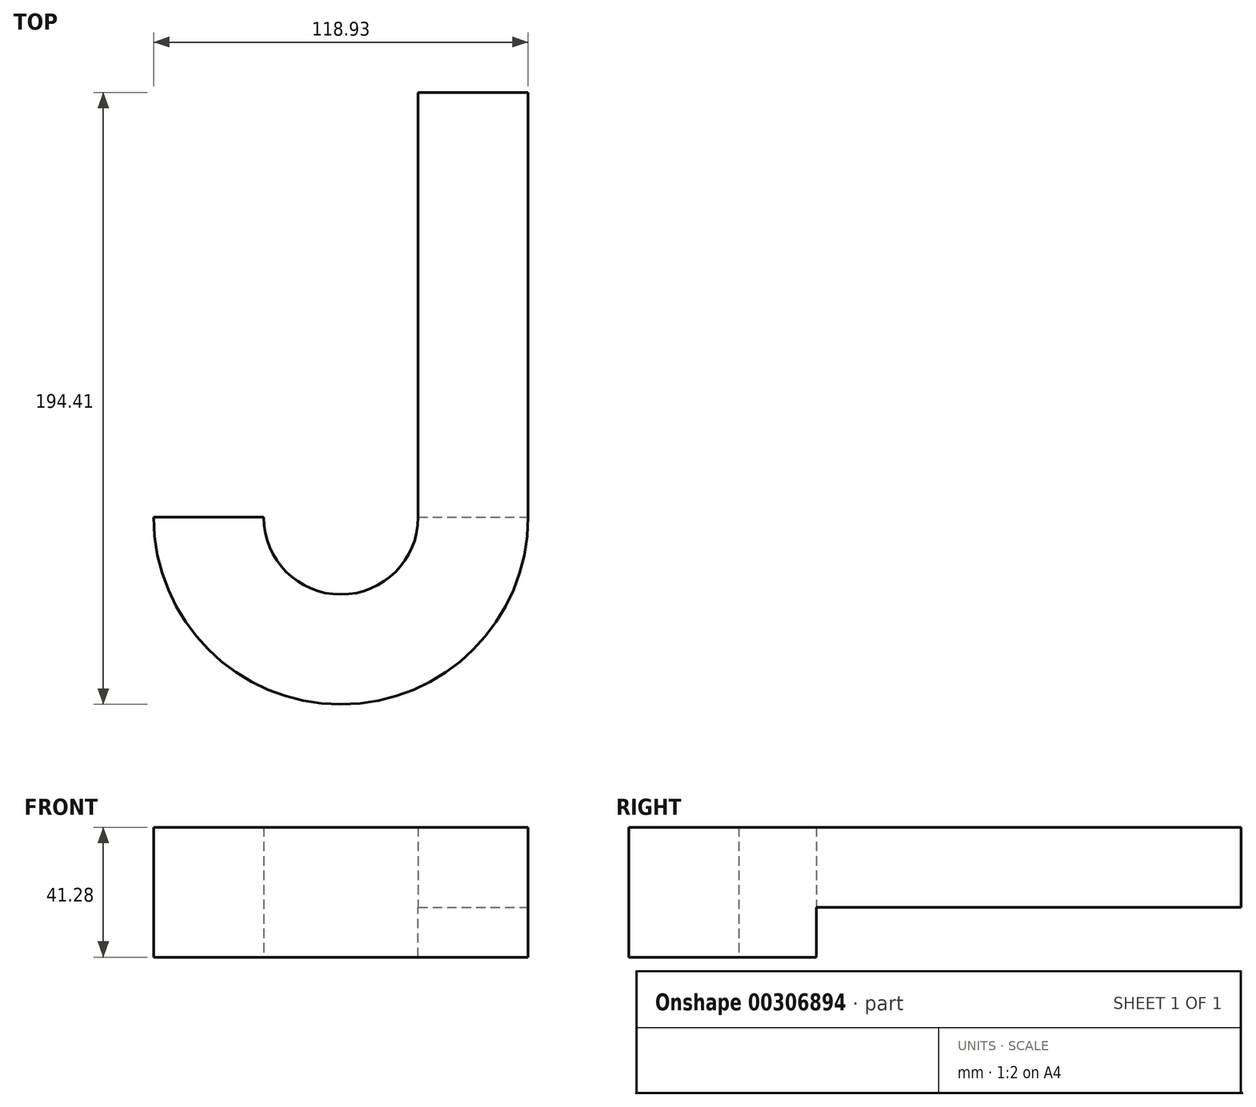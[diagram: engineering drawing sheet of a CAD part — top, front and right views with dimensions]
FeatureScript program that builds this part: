
annotation { "Feature Type Name" : "Feature", "Feature Type Description" : "" }
export const myFeature = defineFeature(function(context is Context, id is Id, definition is map)
    precondition{}
    {
        {
            var Q0;
            Q0=qCreatedBy(makeId("Top.planeOp"),FACE);
            var sketch = newSketch(context, id + "F0", { "sketchPlane" : qUnion([Q0])});
            skLineSegment(sketch, "E0.bottom", {"start": v(-17.46, 67.47) * mm, "end": v(17.46, 67.47) * mm});
            skLineSegment(sketch, "E0.top", {"start": v(-17.46, -67.47) * mm, "end": v(17.46, -67.47) * mm});
            skLineSegment(sketch, "E0.left", {"start": v(-17.46, 67.47) * mm, "end": v(-17.46, -67.47) * mm});
            skLineSegment(sketch, "E0.right", {"start": v(17.46, 67.47) * mm, "end": v(17.46, -67.47) * mm});
            skPoint(sketch, "E0.middle", {"position": v(0, 0) * mm});
            skArc(sketch, "E1", {"start": v(17.46, -67.47) * mm, "mid": v(-42, -126.94) * mm, "end": v(-101.47, -67.47) * mm});
            skArc(sketch, "E2.0", {"start": v(-17.46, -67.47) * mm, "mid": v(-42, -92.01) * mm, "end": v(-66.55, -67.47) * mm});
            skLineSegment(sketch, "E3", {"start": v(-66.55, -67.47) * mm, "end": v(-101.47, -67.47) * mm});
            skSolve(sketch);
        }
        {
            var Q0;
            Q0=makeQuery(id+"F0.imprint","IMPRINT",FACE,{"disambiguationData":[TD([[makeQuery(id+"F0.imprint","IMPRINT",EDGE,{"derivedFrom":sQuery(id+"F0.wireOp",EDGE,"E0.bottom")}),-1.0]])]});
            extrude(context, id + "F1", {"entities" : qUnion([Q0]), "depth" : 25.4 * mm});
        }
        {
            var Q0;
            Q0 = qSketchRegion(id + "F0", true);
            extrude(context, id + "F2", {"entities" : qUnion([Q0]), "operationType" : NewBodyOperationType.ADD, "depth" : 25.4 * mm});
        }
        {
            var Q0;
            {var subQ0=sQuery(id+"F0.wireOp",EDGE,"E0.right");var subQ1=sQuery(id+"F0.wireOp",EDGE,"E0.left");var subQ2=sQuery(id+"F0.wireOp",EDGE,"E0.bottom");Q0=makeQuery(id+"F2.boolean.opBoolean","MERGE",FACE,{"derivedFrom":[makeQuery(id+"F1.opExtrude","CAP_FACE",FACE,{"disambiguationData":[OSD([subQ2,sQuery(id+"F0.wireOp",EDGE,"E0.top"),subQ1,subQ0])],"isStart":true}),makeQuery(id+"F2.opExtrude","CAP_FACE",FACE,{"disambiguationData":[OSD([subQ2,subQ1,subQ0,sQuery(id+"F0.wireOp",EDGE,"E1"),sQuery(id+"F0.wireOp",EDGE,"E2.0"),sQuery(id+"F0.wireOp",EDGE,"E3")])],"isStart":true})]});}
            var sketch = newSketch(context, id + "F3", { "sketchPlane" : qUnion([Q0])});
            skLineSegment(sketch, "E4", {"start": v(-17.46, 67.47) * mm, "end": v(17.46, 67.47) * mm});
            skSolve(sketch);
        }
        {
            var Q0;
            Q0=makeQuery(id+"F3.imprint","IMPRINT",FACE,{"disambiguationData":[TD([[makeQuery(id+"F3.imprint","IMPRINT",EDGE,{"derivedFrom":sQuery(id+"F3.wireOp",EDGE,"E4")}),1.0]])]});
            extrude(context, id + "F4", {"entities" : qUnion([Q0]), "operationType" : NewBodyOperationType.ADD, "depth" : 15.88 * mm});
        }
    });
